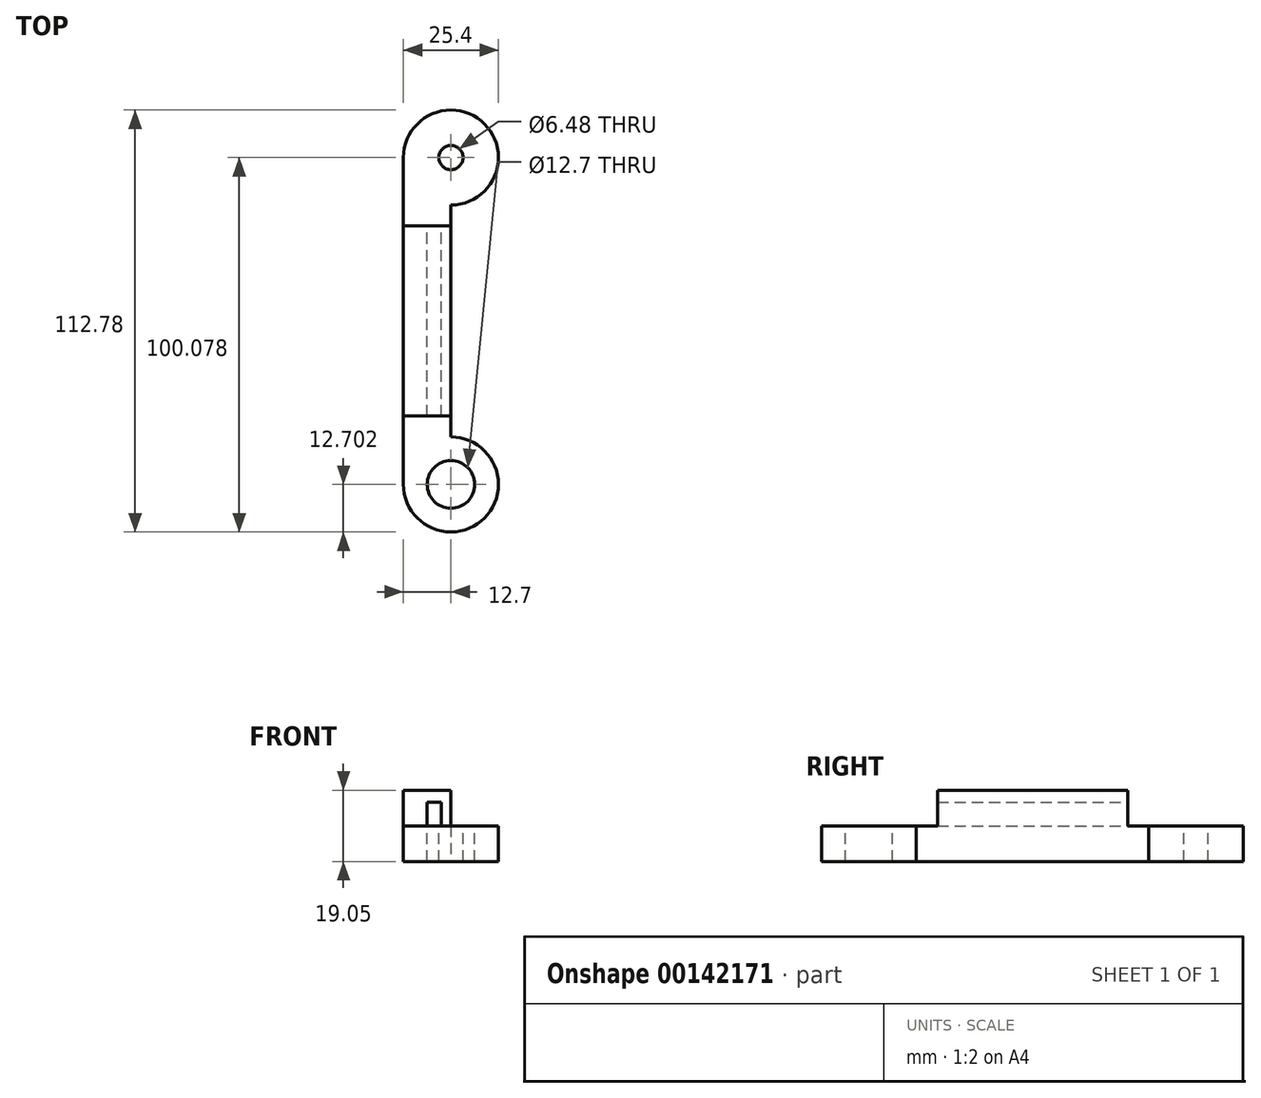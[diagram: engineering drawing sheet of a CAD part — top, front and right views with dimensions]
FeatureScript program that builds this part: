
annotation { "Feature Type Name" : "Feature", "Feature Type Description" : "" }
export const myFeature = defineFeature(function(context is Context, id is Id, definition is map)
    precondition{}
    {
        {
            var Q0;
            Q0=qCreatedBy(makeId("Top.planeOp"),FACE);
            var sketch = newSketch(context, id + "F0", { "sketchPlane" : qUnion([Q0])});
            skCircle(sketch, "E0", {"center": v(0, 43.69) * mm, "radius": 12.7 * mm});
            skCircle(sketch, "E1", {"center": v(0, -43.69) * mm, "radius": 12.7 * mm});
            skLineSegment(sketch, "E2", {"start": v(0, 43.69) * mm, "end": v(0, -43.69) * mm, "construction": true});
            skLineSegment(sketch, "E3", {"start": v(0, 30.99) * mm, "end": v(0, -30.99) * mm});
            skLineSegment(sketch, "E4", {"start": v(-12.7, 43.69) * mm, "end": v(-12.7, -43.69) * mm});
            skLineSegment(sketch, "E5", {"start": v(0, 43.69) * mm, "end": v(-12.7, 43.69) * mm, "construction": true});
            skSolve(sketch);
        }
        {
            var Q0;
            {var subQ0=sQuery(id+"F0.wireOp",EDGE,"E1");var subQ1=makeQuery(id+"F0.imprint","INTERSECT",VERTEX,{"derivedFrom":[subQ0,sQuery(id+"F0.wireOp",EDGE,"E3")]});Q0=makeQuery(id+"F0.imprint","IMPRINT",FACE,{"disambiguationData":[TD([[makeQuery(id+"F0.imprint","IMPRINT",EDGE,{"disambiguationData":[TD([[subQ1,-1.0]])],"derivedFrom":subQ0}),1.0]])]});}
            var Q1;
            {var subQ0=sQuery(id+"F0.wireOp",EDGE,"E3");Q1=makeQuery(id+"F0.imprint","IMPRINT",FACE,{"disambiguationData":[TD([[makeQuery(id+"F0.imprint","IMPRINT",EDGE,{"derivedFrom":subQ0}),-1.0]])]});}
            var Q2;
            {var subQ0=sQuery(id+"F0.wireOp",EDGE,"E0");var subQ1=makeQuery(id+"F0.imprint","INTERSECT",VERTEX,{"derivedFrom":[subQ0,sQuery(id+"F0.wireOp",EDGE,"E3")]});Q2=makeQuery(id+"F0.imprint","IMPRINT",FACE,{"disambiguationData":[TD([[makeQuery(id+"F0.imprint","IMPRINT",EDGE,{"disambiguationData":[TD([[subQ1,1.0]])],"derivedFrom":subQ0}),1.0]])]});}
            extrude(context, id + "F1", {"entities" : qUnion([Q0, Q1, Q2]), "depth" : 9.52 * mm});
        }
        {
            var Q0;
            Q0=makeQuery(id+"F1.opExtrude","CAP_FACE",FACE,{"disambiguationData":[OSD([sQuery(id+"F0.wireOp",EDGE,"E0"),sQuery(id+"F0.wireOp",EDGE,"E1"),sQuery(id+"F0.wireOp",EDGE,"E3"),sQuery(id+"F0.wireOp",EDGE,"E4")])],"isStart":false});
            var sketch = newSketch(context, id + "F2", { "sketchPlane" : qUnion([Q0])});
            skCircle(sketch, "E6", {"center": v(0, -43.69) * mm, "radius": 6.35 * mm});
            skCircle(sketch, "E7", {"center": v(0, 43.69) * mm, "radius": 3.24 * mm});
            skSolve(sketch);
        }
        {
            var Q0;
            Q0=makeQuery(id+"F2.imprint","IMPRINT",FACE,{"disambiguationData":[TD([[makeQuery(id+"F2.imprint","IMPRINT",EDGE,{"derivedFrom":sQuery(id+"F2.wireOp",EDGE,"E6")}),1.0]])]});
            var Q1;
            Q1=makeQuery(id+"F2.imprint","IMPRINT",FACE,{"disambiguationData":[TD([[makeQuery(id+"F2.imprint","IMPRINT",EDGE,{"derivedFrom":sQuery(id+"F2.wireOp",EDGE,"E7")}),1.0]])]});
            extrude(context, id + "F3", {"entities" : qUnion([Q0, Q1]), "operationType" : NewBodyOperationType.REMOVE, "oppositeDirection" : true, "depth" : 25.4 * mm});
        }
        {
            var Q0;
            Q0=qCreatedBy(makeId("Front.planeOp"),FACE);
            var sketch = newSketch(context, id + "F4", { "sketchPlane" : qUnion([Q0])});
            skLineSegment(sketch, "E8.top", {"start": v(-12.7, 19.05) * mm, "end": v(0, 19.05) * mm});
            skLineSegment(sketch, "E8.left", {"start": v(-12.7, 19.05) * mm, "end": v(-12.7, 9.52) * mm});
            skLineSegment(sketch, "E8.right", {"start": v(0, 19.05) * mm, "end": v(0, 9.52) * mm});
            skLineSegment(sketch, "E9", {"start": v(-12.7, 9.53) * mm, "end": v(0, 9.53) * mm});
            skPoint(sketch, "E10.orphan", {"position": v(0, 0) * mm});
            skPoint(sketch, "E11.orphan", {"position": v(-12.7, 0) * mm});
            skLineSegment(sketch, "E12.bottom", {"start": v(-6.35, 9.53) * mm, "end": v(-2.54, 9.53) * mm});
            skLineSegment(sketch, "E12.top", {"start": v(-6.35, 15.88) * mm, "end": v(-2.54, 15.88) * mm});
            skLineSegment(sketch, "E12.left", {"start": v(-6.35, 9.53) * mm, "end": v(-6.35, 15.88) * mm});
            skLineSegment(sketch, "E12.right", {"start": v(-2.54, 9.53) * mm, "end": v(-2.54, 15.88) * mm});
            skSolve(sketch);
        }
        {
            var Q0;
            Q0=makeQuery(id+"F4.imprint","IMPRINT",FACE,{"disambiguationData":[TD([[makeQuery(id+"F4.imprint","IMPRINT",EDGE,{"derivedFrom":sQuery(id+"F4.wireOp",EDGE,"E8.top")}),-1.0]])]});
            extrude(context, id + "F5", {"entities" : qUnion([Q0]), "operationType" : NewBodyOperationType.ADD, "endBound" : BoundingType.SYMMETRIC, "depth" : 50.8 * mm});
        }
    });
